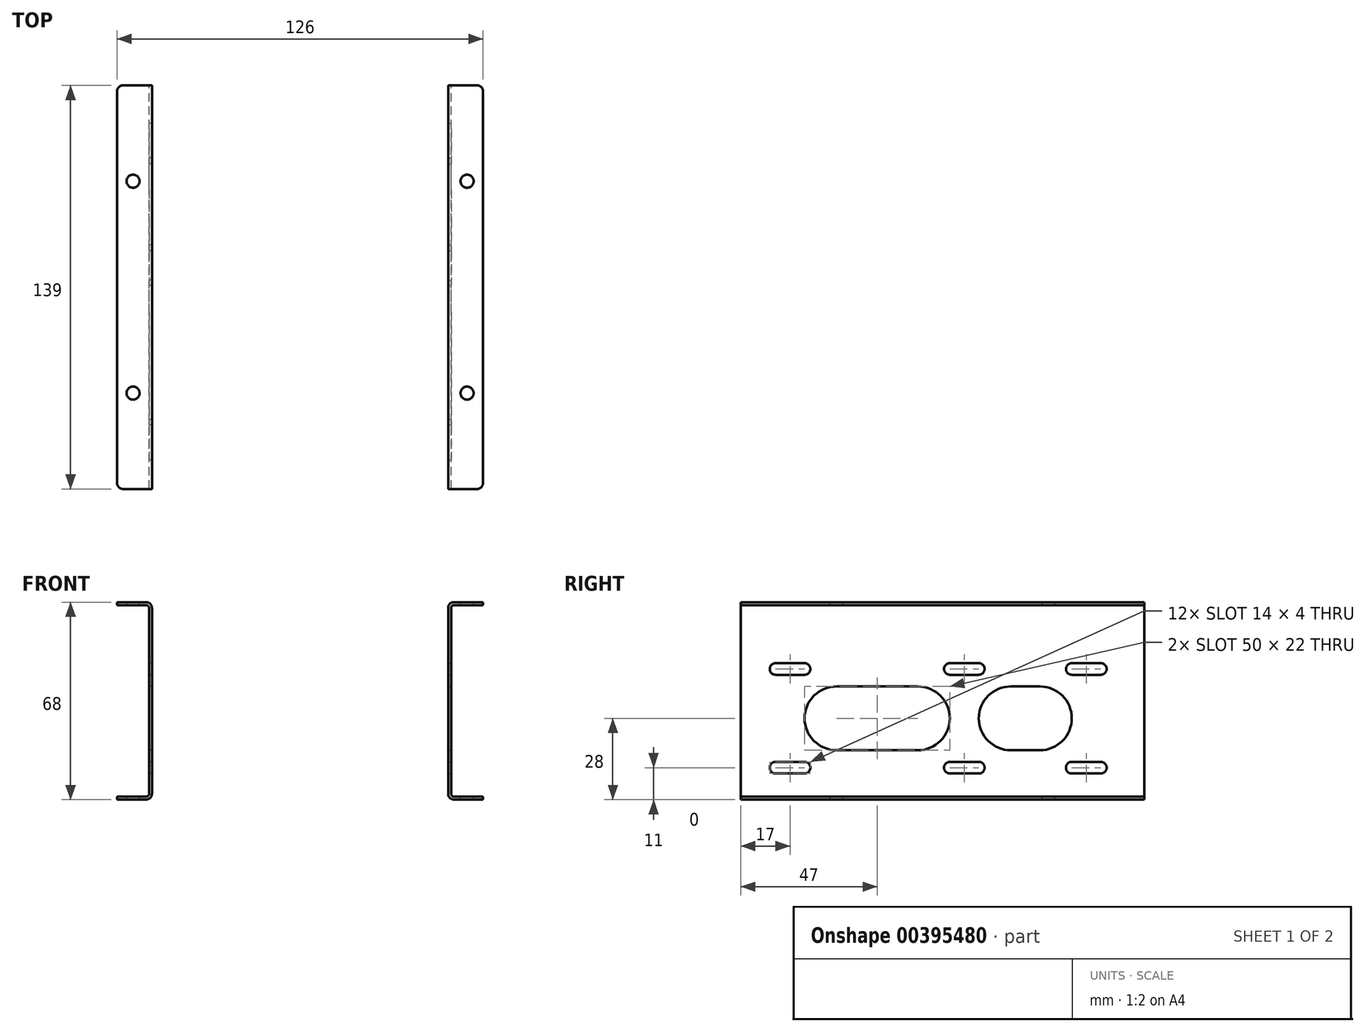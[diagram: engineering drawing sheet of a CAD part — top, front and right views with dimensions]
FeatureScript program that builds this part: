
annotation { "Feature Type Name" : "Feature", "Feature Type Description" : "" }
export const myFeature = defineFeature(function(context is Context, id is Id, definition is map)
    precondition{}
    {
        {
            var Q0;
            Q0=qCreatedBy(makeId("Front.planeOp"),FACE);
            var sketch = newSketch(context, id + "F0", { "sketchPlane" : qUnion([Q0])});
            skLineSegment(sketch, "E0", {"start": v(0, 0) * mm, "end": v(10, 0) * mm});
            skLineSegment(sketch, "E1", {"start": v(12, 2) * mm, "end": v(12, 66) * mm});
            skLineSegment(sketch, "E2", {"start": v(10, 68) * mm, "end": v(0, 68) * mm});
            skLineSegment(sketch, "E3.0", {"start": v(0, 1) * mm, "end": v(10, 1) * mm});
            skLineSegment(sketch, "E4.0", {"start": v(11, 2) * mm, "end": v(11, 66) * mm});
            skLineSegment(sketch, "E5.0", {"start": v(10, 67) * mm, "end": v(0, 67) * mm});
            skLineSegment(sketch, "E6", {"start": v(0, 67) * mm, "end": v(0, 68) * mm});
            skLineSegment(sketch, "E7", {"start": v(0, 0) * mm, "end": v(0, 1) * mm});
            skPoint(sketch, "E8.visualSharp", {"position": v(11, 1) * mm});
            skArc(sketch, "E8.filletArc", {"start": v(10, 1) * mm, "mid": v(10.7, 1.3) * mm, "end": v(11, 2) * mm});
            skPoint(sketch, "E9.visualSharp", {"position": v(12, 0) * mm});
            skArc(sketch, "E9.filletArc", {"start": v(10, 0) * mm, "mid": v(11.41, 0.59) * mm, "end": v(12, 2) * mm});
            skPoint(sketch, "E10.visualSharp", {"position": v(11, 67) * mm});
            skArc(sketch, "E10.filletArc", {"start": v(11, 66) * mm, "mid": v(10.7, 66.7) * mm, "end": v(10, 67) * mm});
            skPoint(sketch, "E11.visualSharp", {"position": v(12, 68) * mm});
            skArc(sketch, "E11.filletArc", {"start": v(12, 66) * mm, "mid": v(11.41, 67.41) * mm, "end": v(10, 68) * mm});
            skSolve(sketch);
        }
        {
            var Q0;
            Q0=qSketchRegion(id+"F0",true);
            extrude(context, id + "F1", {"entities" : qUnion([Q0]), "depth" : 139 * mm});
        }
        {
            var Q0;
            Q0=makeQuery(id+"F1.opExtrude","SWEPT_FACE",FACE,{"disambiguationData":[OSD([sQuery(id+"F0.wireOp",EDGE,"E2")])]});
            var sketch = newSketch(context, id + "F2", { "sketchPlane" : qUnion([Q0])});
            skCircle(sketch, "E12", {"center": v(5.5, -33) * mm, "radius": 2.25 * mm});
            skCircle(sketch, "E13.0.1.0", {"center": v(5.5, -106) * mm, "radius": 2.25 * mm});
            skLineSegment(sketch, "E13.direction1", {"start": v(5.5, -33) * mm, "end": v(30.5, -33) * mm, "construction": true});
            skLineSegment(sketch, "E13.direction2", {"start": v(5.5, -33) * mm, "end": v(5.5, -106) * mm, "construction": true});
            skSolve(sketch);
        }
        {
            var Q0;
            Q0=sQuery(id+"F2.wireOp",VERTEX,"E13.0.1.0.center");
            var Q1;
            Q1=sQuery(id+"F2.wireOp",VERTEX,"E12.center");
            var Q2;
            Q2=makeQuery(id+"F1.opExtrude","SWEPT_BODY",BODY,{"disambiguationData":[OSD([sQuery(id+"F0.wireOp",EDGE,"E0"),sQuery(id+"F0.wireOp",EDGE,"E1"),sQuery(id+"F0.wireOp",EDGE,"E2"),sQuery(id+"F0.wireOp",EDGE,"E3.0"),sQuery(id+"F0.wireOp",EDGE,"E4.0"),sQuery(id+"F0.wireOp",EDGE,"E5.0"),sQuery(id+"F0.wireOp",EDGE,"E6"),sQuery(id+"F0.wireOp",EDGE,"E7"),sQuery(id+"F0.wireOp",EDGE,"E8.filletArc"),sQuery(id+"F0.wireOp",EDGE,"E9.filletArc"),sQuery(id+"F0.wireOp",EDGE,"E10.filletArc"),sQuery(id+"F0.wireOp",EDGE,"E11.filletArc")])]});
            hole(context, id + "F3", {"style" : HoleStyle.SIMPLE, "endStyle" : HoleEndStyle.THROUGH, "holeDiameter" : 4.5 * mm, "isTappedThrough" : true, "tappedDepth" : 12 * mm, "tapClearance" : 3, "locations" : qUnion([Q0, Q1]), "scope" : qUnion([Q2])});
        }
        {
            var Q0;
            Q0=makeQuery(id+"F1.opExtrude","SWEPT_FACE",FACE,{"disambiguationData":[OSD([sQuery(id+"F0.wireOp",EDGE,"E4.0")])]});
            var sketch = newSketch(context, id + "F4", { "sketchPlane" : qUnion([Q0])});
            skLineSegment(sketch, "E14", {"start": v(15, 13) * mm, "end": v(25, 13) * mm});
            skLineSegment(sketch, "E15", {"start": v(15, 9) * mm, "end": v(25, 9) * mm});
            skArc(sketch, "E16", {"start": v(25, 13) * mm, "mid": v(27, 11) * mm, "end": v(25, 9) * mm});
            skArc(sketch, "E17", {"start": v(15, 13) * mm, "mid": v(13, 11) * mm, "end": v(15, 9) * mm});
            skPoint(sketch, "E18", {"position": v(20, 11) * mm});
            skPoint(sketch, "E19.0.1.0", {"position": v(20, 45) * mm});
            skArc(sketch, "E19.0.1.1", {"start": v(15, 47) * mm, "mid": v(13, 45) * mm, "end": v(15, 43) * mm});
            skLineSegment(sketch, "E19.0.1.2", {"start": v(15, 47) * mm, "end": v(25, 47) * mm});
            skLineSegment(sketch, "E19.0.1.3", {"start": v(15, 43) * mm, "end": v(25, 43) * mm});
            skArc(sketch, "E19.0.1.4", {"start": v(25, 47) * mm, "mid": v(27, 45) * mm, "end": v(25, 43) * mm});
            skPoint(sketch, "E19.1.0.0", {"position": v(62, 11) * mm});
            skArc(sketch, "E19.1.0.1", {"start": v(57, 13) * mm, "mid": v(55, 11) * mm, "end": v(57, 9) * mm});
            skLineSegment(sketch, "E19.1.0.2", {"start": v(57, 13) * mm, "end": v(67, 13) * mm});
            skLineSegment(sketch, "E19.1.0.3", {"start": v(57, 9) * mm, "end": v(67, 9) * mm});
            skArc(sketch, "E19.1.0.4", {"start": v(67, 13) * mm, "mid": v(69, 11) * mm, "end": v(67, 9) * mm});
            skPoint(sketch, "E19.1.1.0", {"position": v(62, 45) * mm});
            skArc(sketch, "E19.1.1.1", {"start": v(57, 47) * mm, "mid": v(55, 45) * mm, "end": v(57, 43) * mm});
            skLineSegment(sketch, "E19.1.1.2", {"start": v(57, 47) * mm, "end": v(67, 47) * mm});
            skLineSegment(sketch, "E19.1.1.3", {"start": v(57, 43) * mm, "end": v(67, 43) * mm});
            skArc(sketch, "E19.1.1.4", {"start": v(67, 47) * mm, "mid": v(69, 45) * mm, "end": v(67, 43) * mm});
            skLineSegment(sketch, "E19.direction1", {"start": v(20, 11) * mm, "end": v(62, 11) * mm, "construction": true});
            skLineSegment(sketch, "E19.direction2", {"start": v(20, 11) * mm, "end": v(20, 45) * mm, "construction": true});
            skPoint(sketch, "E20.1.0.0", {"position": v(122, 11) * mm});
            skLineSegment(sketch, "E20.1.0.1", {"start": v(117, 13) * mm, "end": v(127, 13) * mm});
            skArc(sketch, "E20.1.0.2", {"start": v(117, 13) * mm, "mid": v(115, 11) * mm, "end": v(117, 9) * mm});
            skLineSegment(sketch, "E20.1.0.3", {"start": v(117, 9) * mm, "end": v(127, 9) * mm});
            skArc(sketch, "E20.1.0.4", {"start": v(127, 13) * mm, "mid": v(129, 11) * mm, "end": v(127, 9) * mm});
            skPoint(sketch, "E20.1.1.0", {"position": v(122, 45) * mm});
            skLineSegment(sketch, "E20.1.1.1", {"start": v(117, 47) * mm, "end": v(127, 47) * mm});
            skArc(sketch, "E20.1.1.2", {"start": v(117, 47) * mm, "mid": v(115, 45) * mm, "end": v(117, 43) * mm});
            skLineSegment(sketch, "E20.1.1.3", {"start": v(117, 43) * mm, "end": v(127, 43) * mm});
            skArc(sketch, "E20.1.1.4", {"start": v(127, 47) * mm, "mid": v(129, 45) * mm, "end": v(127, 43) * mm});
            skLineSegment(sketch, "E20.direction1", {"start": v(62, 11) * mm, "end": v(122, 11) * mm, "construction": true});
            skLineSegment(sketch, "E20.direction2", {"start": v(62, 11) * mm, "end": v(62, 45) * mm, "construction": true});
            skSolve(sketch);
        }
        {
            var Q0;
            Q0=qSketchRegion(id+"F4",true);
            extrude(context, id + "F5", {"entities" : qUnion([Q0]), "operationType" : NewBodyOperationType.REMOVE, "oppositeDirection" : true, "depth" : 25 * mm});
        }
        {
            var Q0;
            Q0=makeQuery(id+"F1.opExtrude","CAP_EDGE",EDGE,{"disambiguationData":[OSD([sQuery(id+"F0.wireOp",EDGE,"E6")])],"isStart":false});
            fillet(context, id + "F6", {"entities" : qUnion([Q0]), "radius" : 2 * mm, "tangentPropagation" : true, "allowEdgeOverflow" : false});
        }
        {
            var Q0;
            Q0=makeQuery(id+"F1.opExtrude","CAP_EDGE",EDGE,{"disambiguationData":[OSD([sQuery(id+"F0.wireOp",EDGE,"E7")])],"isStart":false});
            fillet(context, id + "F7", {"entities" : qUnion([Q0]), "radius" : 2 * mm, "allowEdgeOverflow" : false});
        }
        {
            var Q0;
            Q0=makeQuery(id+"F1.opExtrude","CAP_EDGE",EDGE,{"disambiguationData":[OSD([sQuery(id+"F0.wireOp",EDGE,"E7")])],"isStart":true});
            fillet(context, id + "F8", {"entities" : qUnion([Q0]), "radius" : 2 * mm, "tangentPropagation" : true, "allowEdgeOverflow" : false});
        }
        {
            var Q0;
            Q0=makeQuery(id+"F1.opExtrude","CAP_EDGE",EDGE,{"disambiguationData":[OSD([sQuery(id+"F0.wireOp",EDGE,"E6")])],"isStart":true});
            fillet(context, id + "F9", {"entities" : qUnion([Q0]), "radius" : 2 * mm, "tangentPropagation" : true, "allowEdgeOverflow" : false});
        }
        {
            var Q0;
            Q0=makeQuery(id+"F1.opExtrude","SWEPT_FACE",FACE,{"disambiguationData":[OSD([sQuery(id+"F0.wireOp",EDGE,"E4.0")])]});
            var sketch = newSketch(context, id + "F10", { "sketchPlane" : qUnion([Q0])});
            skLineSegment(sketch, "E21", {"start": v(36, 39) * mm, "end": v(46, 39) * mm});
            skLineSegment(sketch, "E22", {"start": v(36, 17) * mm, "end": v(46, 17) * mm});
            skArc(sketch, "E23", {"start": v(36, 39) * mm, "mid": v(25, 28) * mm, "end": v(36, 17) * mm});
            skArc(sketch, "E24", {"start": v(46, 39) * mm, "mid": v(57, 28) * mm, "end": v(46, 17) * mm});
            skPoint(sketch, "E25", {"position": v(41, 28) * mm});
            skLineSegment(sketch, "E26.direction1", {"start": v(36, 17) * mm, "end": v(61, 17) * mm, "construction": true});
            skLineSegment(sketch, "E26.direction2", {"start": v(36, 17) * mm, "end": v(36, 51) * mm, "construction": true});
            skLineSegment(sketch, "E27", {"start": v(78, 39) * mm, "end": v(106, 39) * mm});
            skLineSegment(sketch, "E28", {"start": v(78, 17) * mm, "end": v(106, 17) * mm});
            skArc(sketch, "E29", {"start": v(78, 39) * mm, "mid": v(67, 28) * mm, "end": v(78, 17) * mm});
            skArc(sketch, "E30", {"start": v(106, 39) * mm, "mid": v(117, 28) * mm, "end": v(106, 17) * mm});
            skPoint(sketch, "E31", {"position": v(92, 28) * mm});
            skLineSegment(sketch, "E32.direction1", {"start": v(78, 17) * mm, "end": v(103, 17) * mm, "construction": true});
            skLineSegment(sketch, "E32.direction2", {"start": v(78, 17) * mm, "end": v(78, 51) * mm, "construction": true});
            skSolve(sketch);
        }
        {
            var Q0;
            Q0=qSketchRegion(id+"F10",true);
            extrude(context, id + "F11", {"entities" : qUnion([Q0]), "operationType" : NewBodyOperationType.REMOVE, "oppositeDirection" : true, "depth" : 25 * mm});
        }
        {
            var Q0;
            Q0=qCreatedBy(makeId("Right.planeOp"),FACE);
            cPlane(context, id + "F12", {"entities" : qUnion([Q0]), "cplaneType" : CPlaneType.OFFSET, "offset" : 63 * mm, "width" : 150 * mm, "height" : 150 * mm});
        }
        {
            var Q0;
            Q0=makeQuery(id+"F1.opExtrude","SWEPT_BODY",BODY,{"disambiguationData":[OSD([sQuery(id+"F0.wireOp",EDGE,"E0"),sQuery(id+"F0.wireOp",EDGE,"E1"),sQuery(id+"F0.wireOp",EDGE,"E2"),sQuery(id+"F0.wireOp",EDGE,"E3.0"),sQuery(id+"F0.wireOp",EDGE,"E4.0"),sQuery(id+"F0.wireOp",EDGE,"E5.0"),sQuery(id+"F0.wireOp",EDGE,"E6"),sQuery(id+"F0.wireOp",EDGE,"E7"),sQuery(id+"F0.wireOp",EDGE,"E8.filletArc"),sQuery(id+"F0.wireOp",EDGE,"E9.filletArc"),sQuery(id+"F0.wireOp",EDGE,"E10.filletArc"),sQuery(id+"F0.wireOp",EDGE,"E11.filletArc")])]});
            var Q1;
            Q1=qCreatedBy(id+"F12.planeOp",FACE);
            mirror(context, id + "F13", {"entities" : qUnion([Q0]), "mirrorPlane" : qUnion([Q1])});
        }
    });
